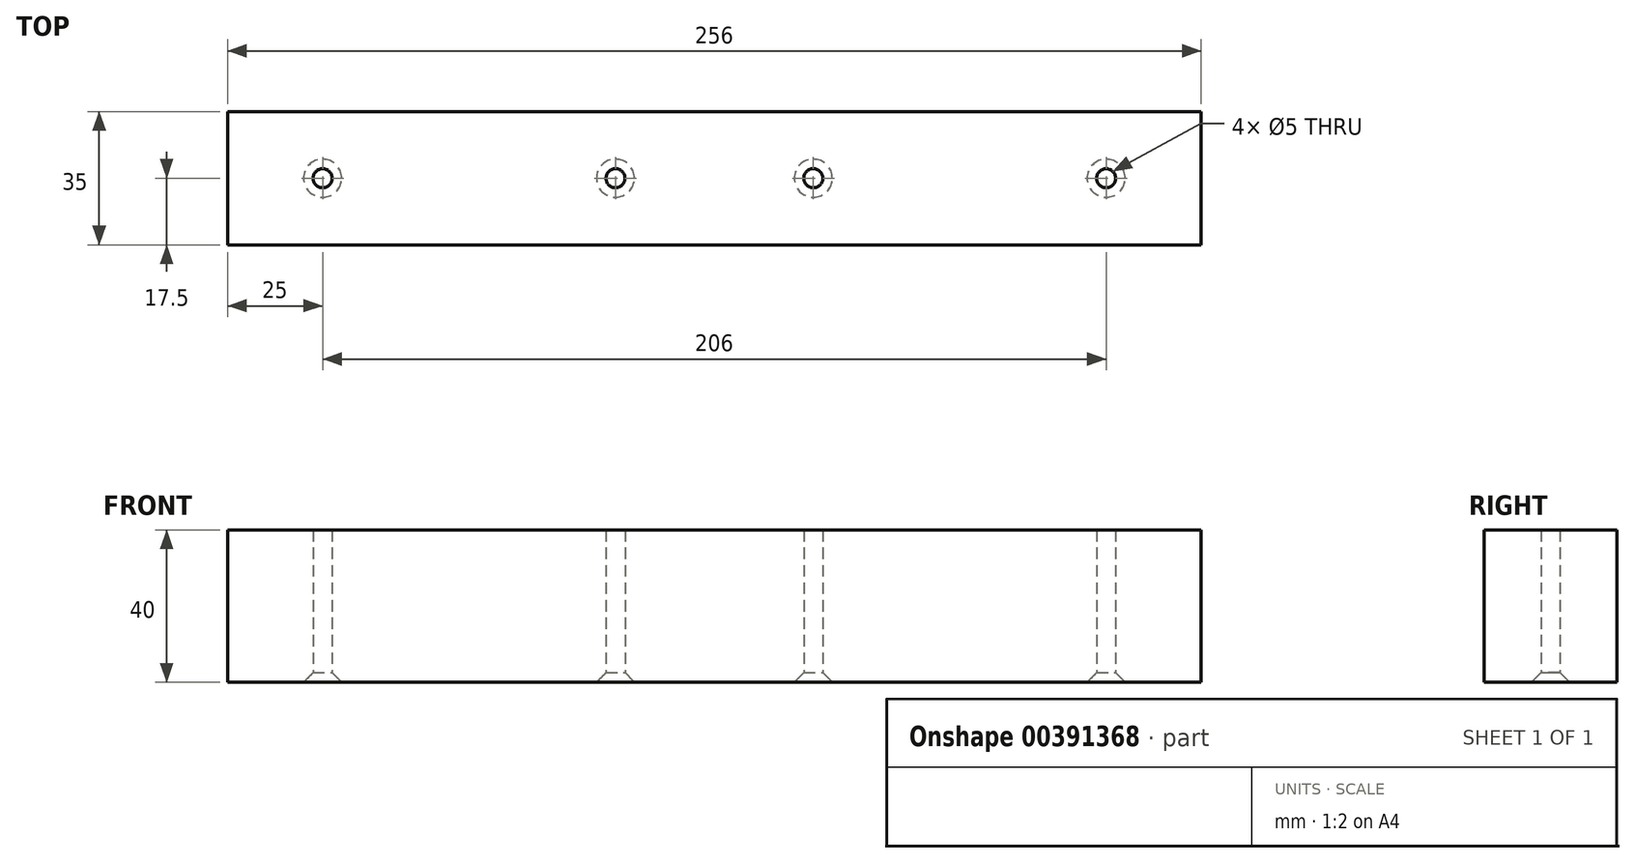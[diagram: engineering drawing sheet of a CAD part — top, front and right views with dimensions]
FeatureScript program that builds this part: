
annotation { "Feature Type Name" : "Feature", "Feature Type Description" : "" }
export const myFeature = defineFeature(function(context is Context, id is Id, definition is map)
    precondition{}
    {
        {
            var Q0;
            Q0=qCreatedBy(makeId("Right.planeOp"),FACE);
            var sketch = newSketch(context, id + "F0", { "sketchPlane" : qUnion([Q0])});
            skLineSegment(sketch, "E0.bottom", {"start": v(35, 47.25) * mm, "end": v(0, 47.25) * mm});
            skLineSegment(sketch, "E0.top", {"start": v(35, 7.25) * mm, "end": v(0, 7.25) * mm});
            skLineSegment(sketch, "E0.left", {"start": v(35, 47.25) * mm, "end": v(35, 7.25) * mm});
            skLineSegment(sketch, "E0.right", {"start": v(0, 47.25) * mm, "end": v(0, 7.25) * mm});
            skSolve(sketch);
        }
        {
            var Q0;
            Q0=qSketchRegion(id+"F0",true);
            extrude(context, id + "F1", {"entities" : qUnion([Q0]), "depth" : 256 * mm});
        }
        {
            var Q0;
            Q0=makeQuery(id+"F1.opExtrude","SWEPT_FACE",FACE,{"disambiguationData":[OSD([sQuery(id+"F0.wireOp",EDGE,"E0.top")])]});
            var sketch = newSketch(context, id + "F2", { "sketchPlane" : qUnion([Q0])});
            skLineSegment(sketch, "E1", {"start": v(256, -17.5) * mm, "end": v(0, -17.5) * mm, "construction": true});
            skPoint(sketch, "E2", {"position": v(231, -17.5) * mm});
            skPoint(sketch, "E3", {"position": v(25, -17.5) * mm});
            skPoint(sketch, "E4", {"position": v(102, -17.5) * mm});
            skPoint(sketch, "E5", {"position": v(154, -17.5) * mm});
            skLineSegment(sketch, "E6", {"start": v(128, -30.68) * mm, "end": v(128, -3.45) * mm, "construction": true});
            skLineSegment(sketch, "E7", {"start": v(128, -10.77) * mm, "end": v(0, -10.77) * mm});
            skLineSegment(sketch, "E8", {"start": v(0, -10.77) * mm, "end": v(128, -10.77) * mm, "construction": true});
            skLineSegment(sketch, "E9", {"start": v(256, -10.77) * mm, "end": v(128, -10.77) * mm, "construction": true});
            skSolve(sketch);
        }
        {
            var Q0;
            Q0=sQuery(id+"F2.wireOp",VERTEX,"E2");
            var Q1;
            Q1=sQuery(id+"F2.wireOp",VERTEX,"E5");
            var Q2;
            Q2=sQuery(id+"F2.wireOp",VERTEX,"E4");
            var Q3;
            Q3=sQuery(id+"F2.wireOp",VERTEX,"E3");
            var Q4;
            Q4=makeQuery(id+"F1.opExtrude","SWEPT_BODY",BODY,{"disambiguationData":[OSD([sQuery(id+"F0.wireOp",EDGE,"E0.bottom"),sQuery(id+"F0.wireOp",EDGE,"E0.top"),sQuery(id+"F0.wireOp",EDGE,"E0.left"),sQuery(id+"F0.wireOp",EDGE,"E0.right")])]});
            hole(context, id + "F3", {"style" : HoleStyle.C_SINK, "endStyle" : HoleEndStyle.THROUGH, "holeDiameter" : 5 * mm, "cSinkDiameter" : 10 * mm, "cSinkAngle" : 90 * degree, "isTappedThrough" : true, "tappedDepth" : 12 * mm, "tapClearance" : 3, "startFromSketch" : true, "locations" : qUnion([Q0, Q1, Q2, Q3]), "scope" : qUnion([Q4])});
        }
    });
